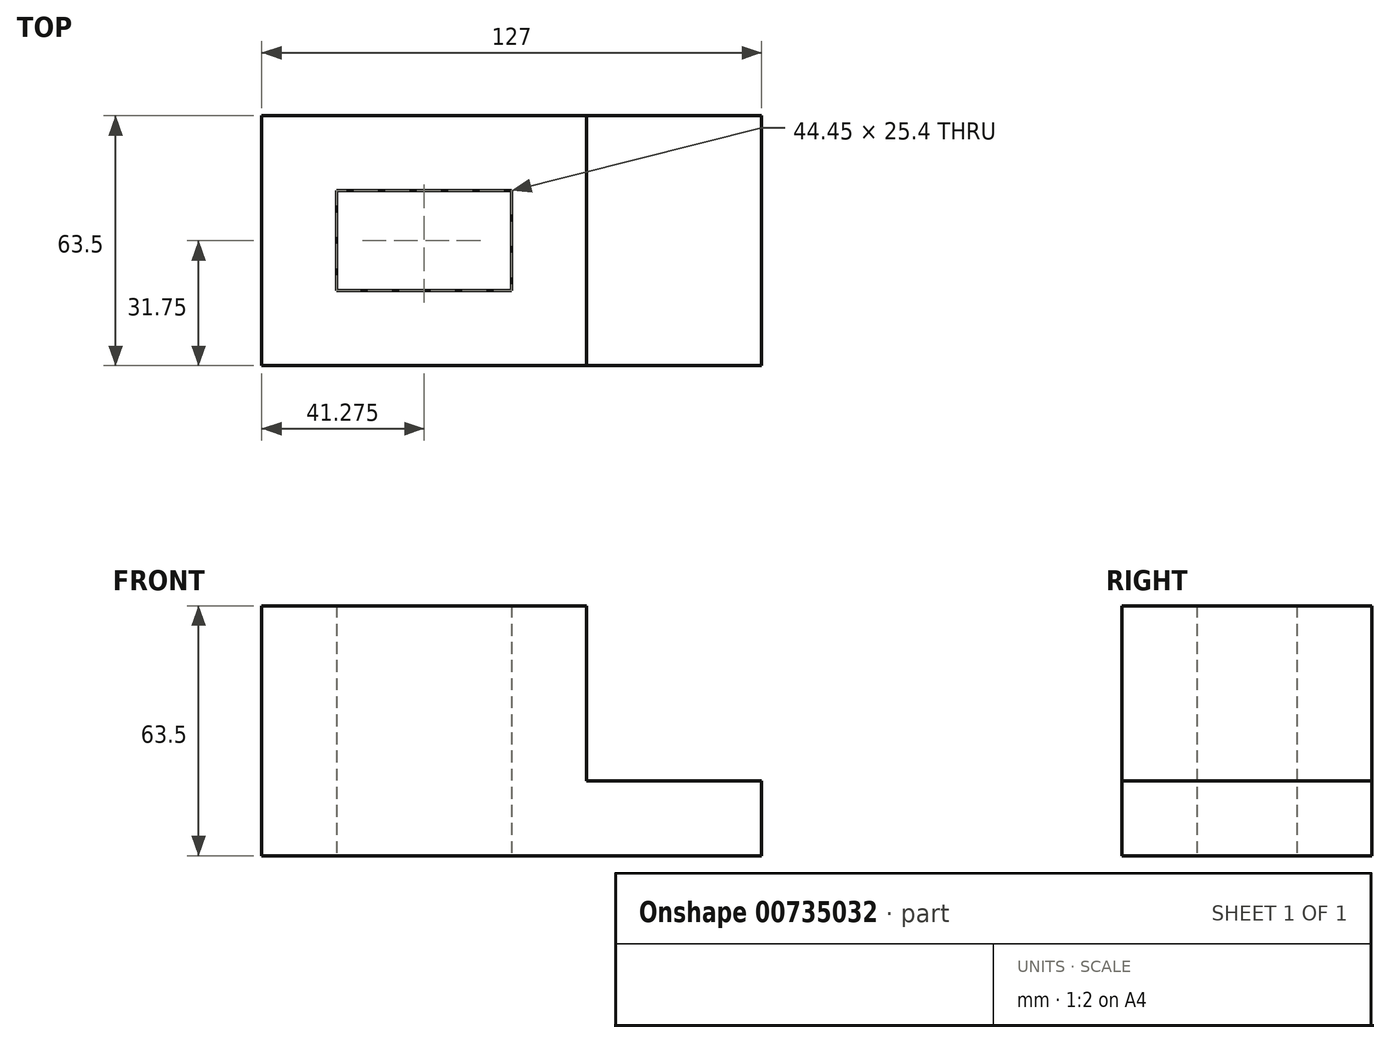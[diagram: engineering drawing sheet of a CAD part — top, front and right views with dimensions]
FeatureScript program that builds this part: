
annotation { "Feature Type Name" : "Feature", "Feature Type Description" : "" }
export const myFeature = defineFeature(function(context is Context, id is Id, definition is map)
    precondition{}
    {
        {
            var Q0;
            Q0=qCreatedBy(makeId("Top.planeOp"),FACE);
            var sketch = newSketch(context, id + "F0", { "sketchPlane" : qUnion([Q0])});
            skLineSegment(sketch, "E0.bottom", {"start": v(0, 0) * mm, "end": v(44.45, 0) * mm});
            skLineSegment(sketch, "E0.top", {"start": v(0, -25.4) * mm, "end": v(44.45, -25.4) * mm});
            skLineSegment(sketch, "E0.left", {"start": v(0, 0) * mm, "end": v(0, -25.4) * mm});
            skLineSegment(sketch, "E0.right", {"start": v(44.45, 0) * mm, "end": v(44.45, -25.4) * mm});
            skLineSegment(sketch, "E1", {"start": v(-19.05, 19.05) * mm, "end": v(-19.05, -44.45) * mm});
            skLineSegment(sketch, "E2", {"start": v(-19.05, -44.45) * mm, "end": v(63.5, -44.45) * mm});
            skLineSegment(sketch, "E3", {"start": v(63.5, -44.45) * mm, "end": v(63.5, 19.05) * mm});
            skLineSegment(sketch, "E4", {"start": v(63.5, 19.05) * mm, "end": v(-19.05, 19.05) * mm});
            skLineSegment(sketch, "E5", {"start": v(63.5, -44.45) * mm, "end": v(107.95, -44.45) * mm});
            skLineSegment(sketch, "E6", {"start": v(63.5, 19.05) * mm, "end": v(107.95, 19.05) * mm});
            skLineSegment(sketch, "E7", {"start": v(107.95, -44.45) * mm, "end": v(107.95, 19.05) * mm});
            skSolve(sketch);
        }
        {
            var Q0;
            Q0=makeQuery(id+"F0.imprint","IMPRINT",FACE,{"disambiguationData":[TD([[makeQuery(id+"F0.imprint","IMPRINT",EDGE,{"derivedFrom":sQuery(id+"F0.wireOp",EDGE,"E0.bottom")}),1.0]])]});
            extrude(context, id + "F1", {"entities" : qUnion([Q0]), "depth" : 63.5 * mm, "offsetDistance" : 25.4 * mm});
        }
        {
            var Q0;
            Q0=makeQuery(id+"F0.imprint","IMPRINT",FACE,{"disambiguationData":[TD([[makeQuery(id+"F0.imprint","IMPRINT",EDGE,{"derivedFrom":sQuery(id+"F0.wireOp",EDGE,"E3")}),-1.0]])]});
            extrude(context, id + "F2", {"entities" : qUnion([Q0]), "operationType" : NewBodyOperationType.ADD, "depth" : 19.05 * mm, "offsetDistance" : 25.4 * mm});
        }
    });
